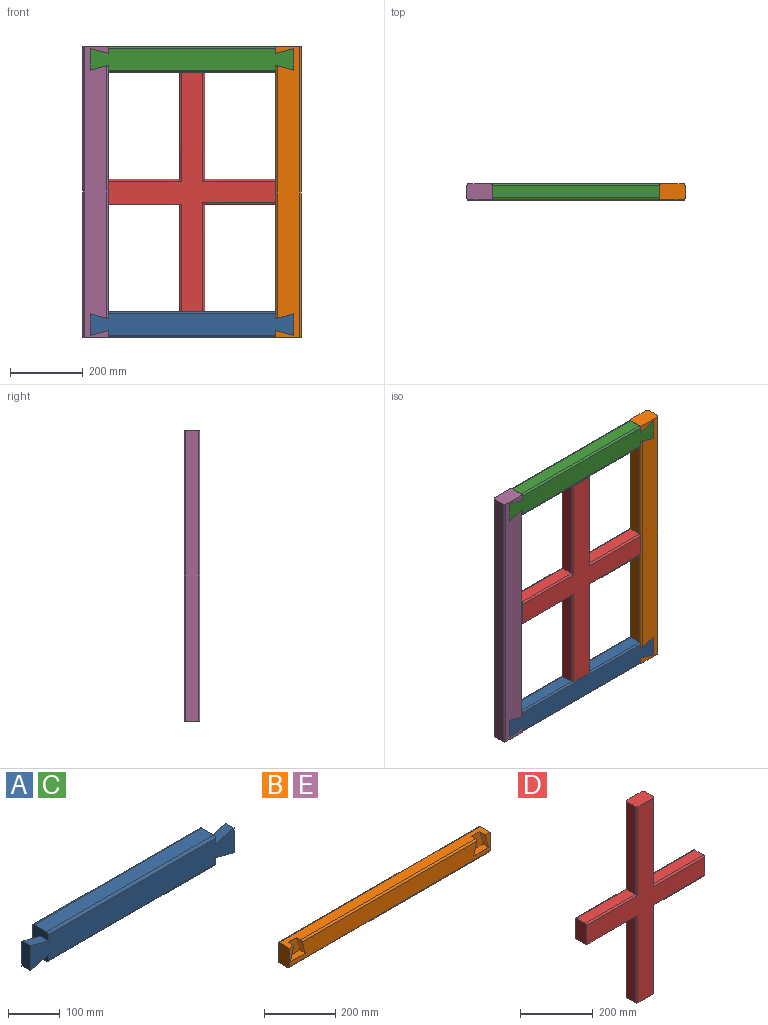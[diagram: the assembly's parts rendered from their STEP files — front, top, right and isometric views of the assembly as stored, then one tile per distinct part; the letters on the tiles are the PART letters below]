
ASSEMBLY  parts=5 mates=4
PART A: 18 faces, bbox 560x44x70 mm
  f0: plane 460x34mm, normal (0,0,-1), area 15640mm2, adj f6,f7,f15,f17
  f1: plane 460x34mm, normal (0,0,1), area 15640mm2, adj f6,f7,f14,f16
  f2: plane 59.28x50mm, normal (0,1,0), area 2294.2mm2, adj f7,f8,f9,f10
  f3: plane 460x60mm, normal (0,1,0), area 27600mm2, adj f6,f7,f16,f17
  f4: plane 560x60mm, normal (0,-1,0), area 32188.5mm2, adj f6,f7,f8,f9,f10,f11,f12,f13
  f5: plane 59.28x50mm, normal (0,1,0), area 2294.2mm2, adj f6,f11,f12,f13
  f6: plane 70x44mm, normal (1,0,0), area 2343.8mm2, adj f0,f1,f3,f4,f5,f11,f13,f14
  f7: plane 70x44mm, normal (-1,0,0), area 2343.8mm2, adj f0,f1,f2,f3,f4,f9,f10,f14
  f8: plane 59.28x22mm, normal (-1,0,0), area 1304.2mm2, adj f2,f4,f9,f10
  f9: plane 50x22mm, normal (0.26,0,0.97), area 1138.8mm2, adj f2,f4,f7,f8
  f10: plane 50x22mm, normal (0.26,0,-0.97), area 1138.8mm2, adj f2,f4,f7,f8
  f11: plane 50x22mm, normal (-0.26,0,0.97), area 1138.8mm2, adj f4,f5,f6,f12
  f12: plane 59.28x22mm, normal (1,0,0), area 1304.2mm2, adj f4,f5,f11,f13
  f13: plane 50x22mm, normal (-0.26,0,-0.97), area 1138.8mm2, adj f4,f5,f6,f12
  f14: cylinder r=5mm len=460mm, axis (1,0,0), area 3612.8mm2, adj f1,f4,f6,f7
  f15: cylinder r=5mm len=460mm, axis (-1,0,0), area 3612.8mm2, adj f0,f4,f6,f7
  f16: cylinder r=5mm len=460mm, axis (-1,0,0), area 3612.8mm2, adj f1,f3,f6,f7
  f17: cylinder r=5mm len=460mm, axis (1,0,0), area 3612.8mm2, adj f0,f3,f6,f7
PART B: 18 faces, bbox 800x44x70 mm
  f0: plane 800x34mm, normal (0,0,-1), area 27200mm2, adj f1,f3,f15,f17
  f1: plane 70x44mm, normal (1,0,0), area 3063.9mm2, adj f0,f2,f4,f5,f15,f16,f17
  f2: plane 800x39mm, normal (0,0,1), area 26283mm2, adj f1,f3,f4,f7,f8,f9,f11,f12
  f3: plane 70x44mm, normal (-1,0,0), area 3063.9mm2, adj f0,f2,f4,f5,f15,f16,f17
  f4: plane 800x65mm, normal (0,-1,0), area 43930.7mm2, adj f1,f2,f3,f6,f7,f8,f10,f11
  f5: plane 800x60mm, normal (0,1,0), area 48000mm2, adj f1,f3,f16,f17
  f6: plane 59.28x22mm, normal (0,0,1), area 1304.2mm2, adj f4,f7,f8,f9
  f7: plane 50x22mm, normal (-0.97,0,-0.26), area 1138.8mm2, adj f2,f4,f6,f9
  f8: plane 50x22mm, normal (0.97,0,-0.26), area 1133.2mm2, adj f2,f4,f6,f9,f14
  f9: plane 59.28x50mm, normal (0,-1,0), area 2294.2mm2, adj f2,f6,f7,f8
  f10: plane 59.28x22mm, normal (0,0,1), area 1304.2mm2, adj f4,f11,f12,f13
  f11: plane 50x22mm, normal (-0.97,0,-0.26), area 1133.2mm2, adj f2,f4,f10,f13,f14
  f12: plane 50x22mm, normal (0.97,0,-0.26), area 1138.8mm2, adj f2,f4,f10,f13
  f13: plane 59.28x50mm, normal (0,-1,0), area 2294.2mm2, adj f2,f10,f11,f12
  f14: cylinder r=5mm len=697.51mm, axis (1,0,0), area 5470.6mm2, adj f2,f4,f8,f11
  f15: cylinder r=5mm len=800mm, axis (-1,0,0), area 6283.2mm2, adj f0,f1,f3,f4
  f16: cylinder r=5mm len=800mm, axis (-1,0,0), area 6283.2mm2, adj f1,f2,f3,f5
  f17: cylinder r=5mm len=800mm, axis (1,0,0), area 6283.2mm2, adj f0,f1,f3,f5
PART C: same geometry as A
PART D: 29 faces, bbox 460x44x660 mm
  f0: plane 195x34mm, normal (0,0,1), area 6630mm2, adj f1,f11,f20,f28
  f1: plane 70x44mm, normal (-1,0,0), area 3063.9mm2, adj f0,f2,f12,f13,f20,f25,f28
  f2: plane 200x39mm, normal (0,0,-1), area 7610.4mm2, adj f1,f3,f12,f18,f25
  f3: plane 295x34mm, normal (-1,0,0), area 10030mm2, adj f2,f4,f18,f26
  f4: plane 70x44mm, normal (0,0,-1), area 3058.5mm2, adj f3,f5,f12,f13,f16,f18,f23,f26
  f5: plane 295x34mm, normal (1,0,0), area 10030mm2, adj f4,f6,f16,f23
  f6: plane 195x34mm, normal (0,0,-1), area 6630mm2, adj f5,f7,f17,f24
  f7: plane 70x44mm, normal (1,0,0), area 3058.5mm2, adj f6,f8,f12,f13,f14,f17,f21,f24
  f8: plane 195x34mm, normal (0,0,1), area 6630mm2, adj f7,f9,f14,f21
  f9: plane 295x34mm, normal (1,0,0), area 10030mm2, adj f8,f10,f15,f22
  f10: plane 70x44mm, normal (0,0,1), area 3058.5mm2, adj f9,f11,f12,f13,f15,f19,f22,f27
  f11: plane 295x34mm, normal (-1,0,0), area 10030mm2, adj f0,f10,f19,f27
  f12: plane 660x460mm, normal (0,-1,0), area 64600mm2, adj f1,f2,f4,f7,f10,f14,f15,f16
  f13: plane 660x460mm, normal (0,1,0), area 63600mm2, adj f1,f4,f7,f10,f21,f22,f23,f24
  f14: cylinder r=5mm len=200mm, axis (1,0,0), area 1545.8mm2, adj f7,f8,f12,f15
  f15: cylinder r=5mm len=300mm, axis (0,0,-1), area 2331.2mm2, adj f9,f10,f12,f14
  f16: cylinder r=5mm len=300mm, axis (0,0,-1), area 2331.2mm2, adj f4,f5,f12,f17
  f17: cylinder r=5mm len=200mm, axis (-1,0,0), area 1545.8mm2, adj f6,f7,f12,f16
  f18: cylinder r=5mm len=295mm, axis (0,0,1), area 2316.9mm2, adj f2,f3,f4,f12
  f19: cylinder r=5mm len=300mm, axis (0,0,1), area 2331.2mm2, adj f10,f11,f12,f20
  f20: cylinder r=5mm len=200mm, axis (1,0,0), area 1545.8mm2, adj f0,f1,f12,f19
  f21: cylinder r=5mm len=200mm, axis (-1,0,0), area 1545.8mm2, adj f7,f8,f13,f22
  f22: cylinder r=5mm len=300mm, axis (0,0,1), area 2331.2mm2, adj f9,f10,f13,f21
  f23: cylinder r=5mm len=300mm, axis (0,0,1), area 2331.2mm2, adj f4,f5,f13,f24
  f24: cylinder r=5mm len=200mm, axis (1,0,0), area 1545.8mm2, adj f6,f7,f13,f23
  f25: cylinder r=5mm len=200mm, axis (1,0,0), area 1545.8mm2, adj f1,f2,f13,f26
  f26: cylinder r=5mm len=300mm, axis (0,0,-1), area 2331.2mm2, adj f3,f4,f13,f25
  f27: cylinder r=5mm len=300mm, axis (0,0,-1), area 2331.2mm2, adj f10,f11,f13,f28
  f28: cylinder r=5mm len=200mm, axis (-1,0,0), area 1545.8mm2, adj f0,f1,f13,f27
PART E: same geometry as B
PLACE A t=(-20.21,104.22,-429.84)mm
PLACE B rot(axis=(0,-1,0),90deg) t=(244.79,104.22,-64.84)mm
PLACE C t=(-20.21,104.22,300.16)mm
PLACE D t=(-20.21,104.22,-64.84)mm
PLACE E rot(axis=(0,1,0),90deg) t=(-285.21,104.22,-64.84)mm
MATE fastened D.f10 <-> C.f0  axis (0,0,1) through (-20.21,82.22,265.16)mm
MATE fastened B.f13 <-> A.f5  axis (0,-1,0) through (259.79,82.22,-400.2)mm
MATE fastened C.f5 <-> B.f9  axis (0,1,0) through (259.79,82.22,329.8)mm
MATE fastened A.f2 <-> E.f9  axis (0,1,0) through (-300.21,82.22,-459.48)mm
